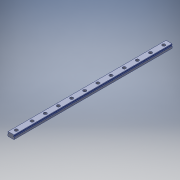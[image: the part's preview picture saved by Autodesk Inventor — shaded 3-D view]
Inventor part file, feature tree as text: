
AUTODESK INVENTOR PART (.ipt)
format: ipt  version: 2019 (Build 230136000, 136)  size: 254,976 bytes
history: native  units: in
note: dims shown in document units (in); Inventor stores cm internally (conversion verified against a paired STEP export)
features: extrude x1, sketch x1, projected_geometry x1, other x1
ambient origin geometry x8: Origin, YZ Plane, XZ Plane, XY Plane, X Axis, Y Axis, Z Axis, Center Point
bodies: Solid1 (feature_tree)
feature tree (4):
  extrude  "Extrusion1"  [1 undecoded]
  sketch  "Sketch1"  dims[d0=5.9055in d1=0.0in]
  projected_geometry  "Projected Loop1"
  other  "Fill Pattern1"
note: 1 required parameter value undecoded (feature->parameter linkage not recoverable at this tier; creation-order binding heuristic only, values carry confidence <= 0.55)
